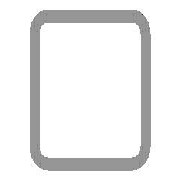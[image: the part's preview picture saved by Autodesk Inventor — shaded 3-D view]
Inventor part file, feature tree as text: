
AUTODESK INVENTOR PART (.ipt)
format: ipt  version: 2022.1 (Build 261234000, 234)  size: 131,584 bytes
history: native  units: mm (DEFAULTED — no unit token found)
features: other x4, sketch x3, extrude x1, plane x1
ambient origin geometry x8: Origin, YZ Plane, XZ Plane, XY Plane, X Axis, Y Axis, Z Axis, Center Point
bodies: Solid1 (feature_tree)
feature tree (9):
  parser-record x1  (decoder bookkeeping rows leaked as tree rows — omitted from the tree; the rows remain in map.json)
  other  "Driven Length"
  other  "Plano inicial"
  other  "Plano final"
  extrude  "Cuerpo"  TaperAngle=0.0deg  [1 undecoded]
  sketch  "Boceto"  dims[d9=40.0mm d11=40.0mm d12=4.0mm d13=-0.0mm d14=450.0mm d15=20.0mm d16=20.0mm d17=90.0deg d18=450.0mm]
  sketch  "Sketch3"  dims[d3=450.0mm d4=0.0mm]
  plane  "Work Plane3"
  sketch  "Sketch4"  dims[d7=8.0mm]
note: 1 required parameter value undecoded (feature->parameter linkage not recoverable at this tier; creation-order binding heuristic only, values carry confidence <= 0.55)
